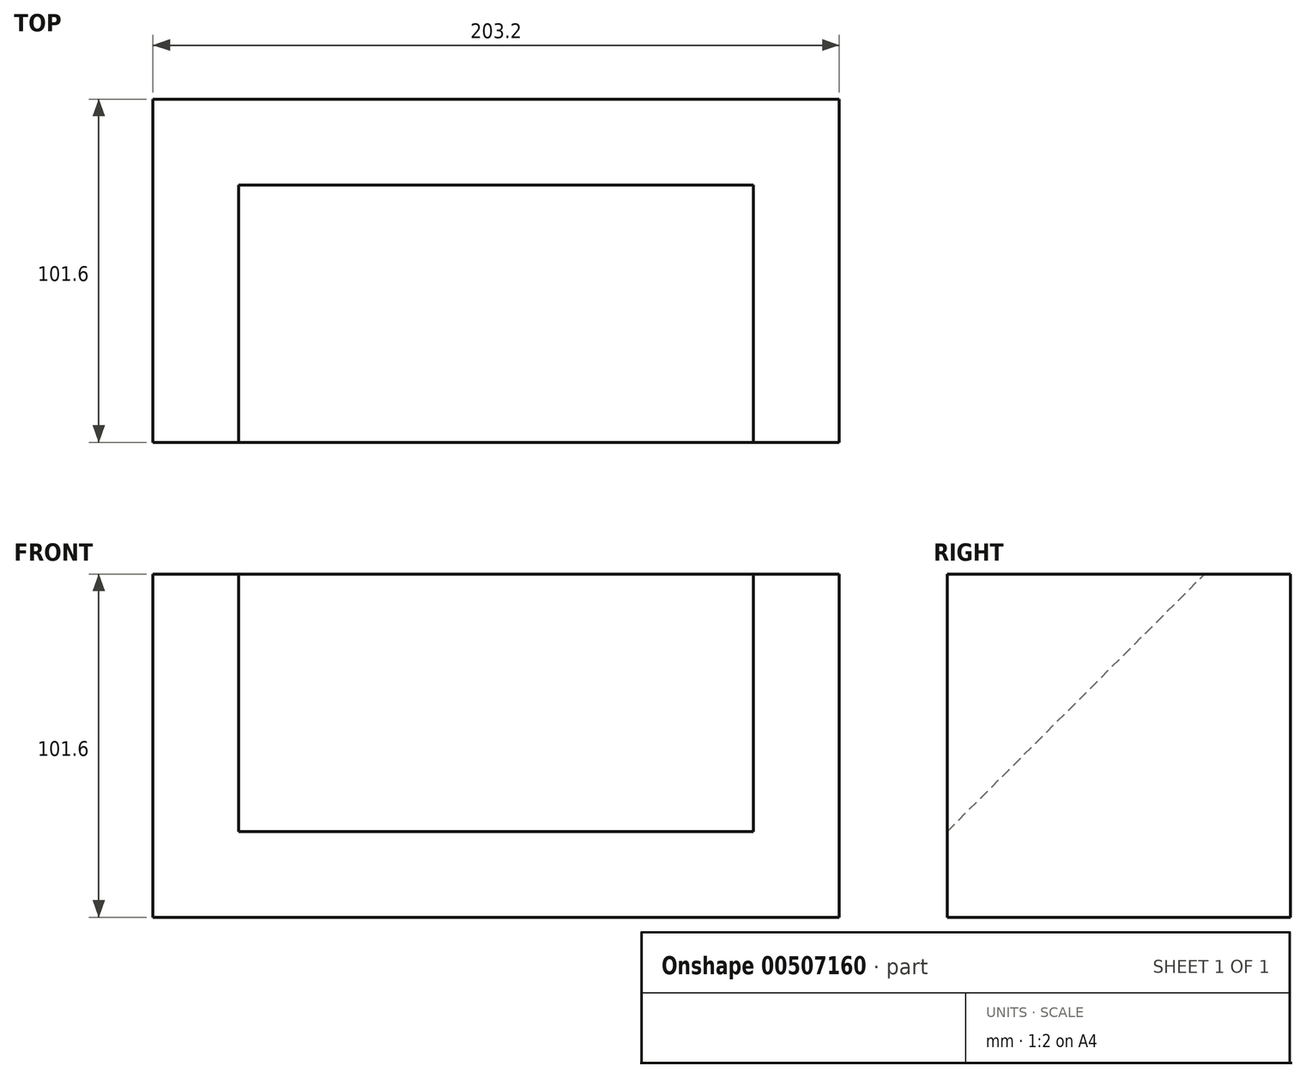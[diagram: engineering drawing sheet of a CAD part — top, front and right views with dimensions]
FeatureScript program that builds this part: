
annotation { "Feature Type Name" : "Feature", "Feature Type Description" : "" }
export const myFeature = defineFeature(function(context is Context, id is Id, definition is map)
    precondition{}
    {
        {
            var Q0;
            Q0=qCreatedBy(makeId("Top.planeOp"),FACE);
            var sketch = newSketch(context, id + "F0", { "sketchPlane" : qUnion([Q0])});
            skLineSegment(sketch, "E0", {"start": v(-67.25, 50.14) * mm, "end": v(-67.25, -51.46) * mm});
            skLineSegment(sketch, "E1", {"start": v(-67.25, -51.46) * mm, "end": v(135.95, -51.46) * mm});
            skLineSegment(sketch, "E2", {"start": v(135.95, -51.46) * mm, "end": v(135.95, 50.14) * mm});
            skLineSegment(sketch, "E3", {"start": v(135.95, 50.14) * mm, "end": v(-67.25, 50.14) * mm});
            skSolve(sketch);
        }
        {
            var Q0;
            Q0 = qSketchRegion(id + "F0", true);
            extrude(context, id + "F1", {"entities" : qUnion([Q0]), "depth" : 101.6 * mm});
        }
        {
            var Q0;
            Q0=makeQuery(id+"F1.opExtrude","CAP_FACE",FACE,{"disambiguationData":[OSD([sQuery(id+"F0.wireOp",EDGE,"E0"),sQuery(id+"F0.wireOp",EDGE,"E1"),sQuery(id+"F0.wireOp",EDGE,"E2"),sQuery(id+"F0.wireOp",EDGE,"E3")])],"isStart":false});
            var sketch = newSketch(context, id + "F2", { "sketchPlane" : qUnion([Q0])});
            skLineSegment(sketch, "E4", {"start": v(-41.85, 24.74) * mm, "end": v(-41.85, -51.46) * mm});
            skLineSegment(sketch, "E5", {"start": v(-41.85, -51.46) * mm, "end": v(110.55, -51.46) * mm});
            skLineSegment(sketch, "E6", {"start": v(110.55, -51.46) * mm, "end": v(110.55, 24.74) * mm});
            skLineSegment(sketch, "E7", {"start": v(110.55, 24.74) * mm, "end": v(-41.85, 24.74) * mm});
            skSolve(sketch);
        }
        {
            var Q0;
            Q0=makeQuery(id+"F2.imprint","IMPRINT",FACE,{"disambiguationData":[TD([[makeQuery(id+"F2.imprint","IMPRINT",EDGE,{"derivedFrom":sQuery(id+"F2.wireOp",EDGE,"E4")}),1.0]])]});
            var Q1;
            Q1 = qSketchRegion(id + "F2", true);
            extrude(context, id + "F3", {"entities" : qUnion([Q0, Q1]), "operationType" : NewBodyOperationType.REMOVE, "oppositeDirection" : true, "depth" : 76.2 * mm});
        }
        {
            var Q0;
            Q0=makeQuery(id+"F3.boolean.opBoolean","COPY",FACE,{"derivedFrom":makeQuery(id+"F3.opExtrude","SWEPT_FACE",FACE,{"disambiguationData":[OSD([sQuery(id+"F2.wireOp",EDGE,"E4")])]})});
            var sketch = newSketch(context, id + "F4", { "sketchPlane" : qUnion([Q0])});
            skLineSegment(sketch, "E8", {"start": v(-51.46, 25.4) * mm, "end": v(24.74, 101.6) * mm});
            skLineSegment(sketch, "E9", {"start": v(24.74, 101.6) * mm, "end": v(24.74, 25.4) * mm});
            skLineSegment(sketch, "E10", {"start": v(24.74, 25.4) * mm, "end": v(-51.46, 25.4) * mm});
            skSolve(sketch);
        }
        {
            var Q0;
            Q0 = qSketchRegion(id + "F4", true);
            extrude(context, id + "F5", {"entities" : qUnion([Q0]), "operationType" : NewBodyOperationType.ADD, "depth" : 152.4 * mm});
        }
    });
